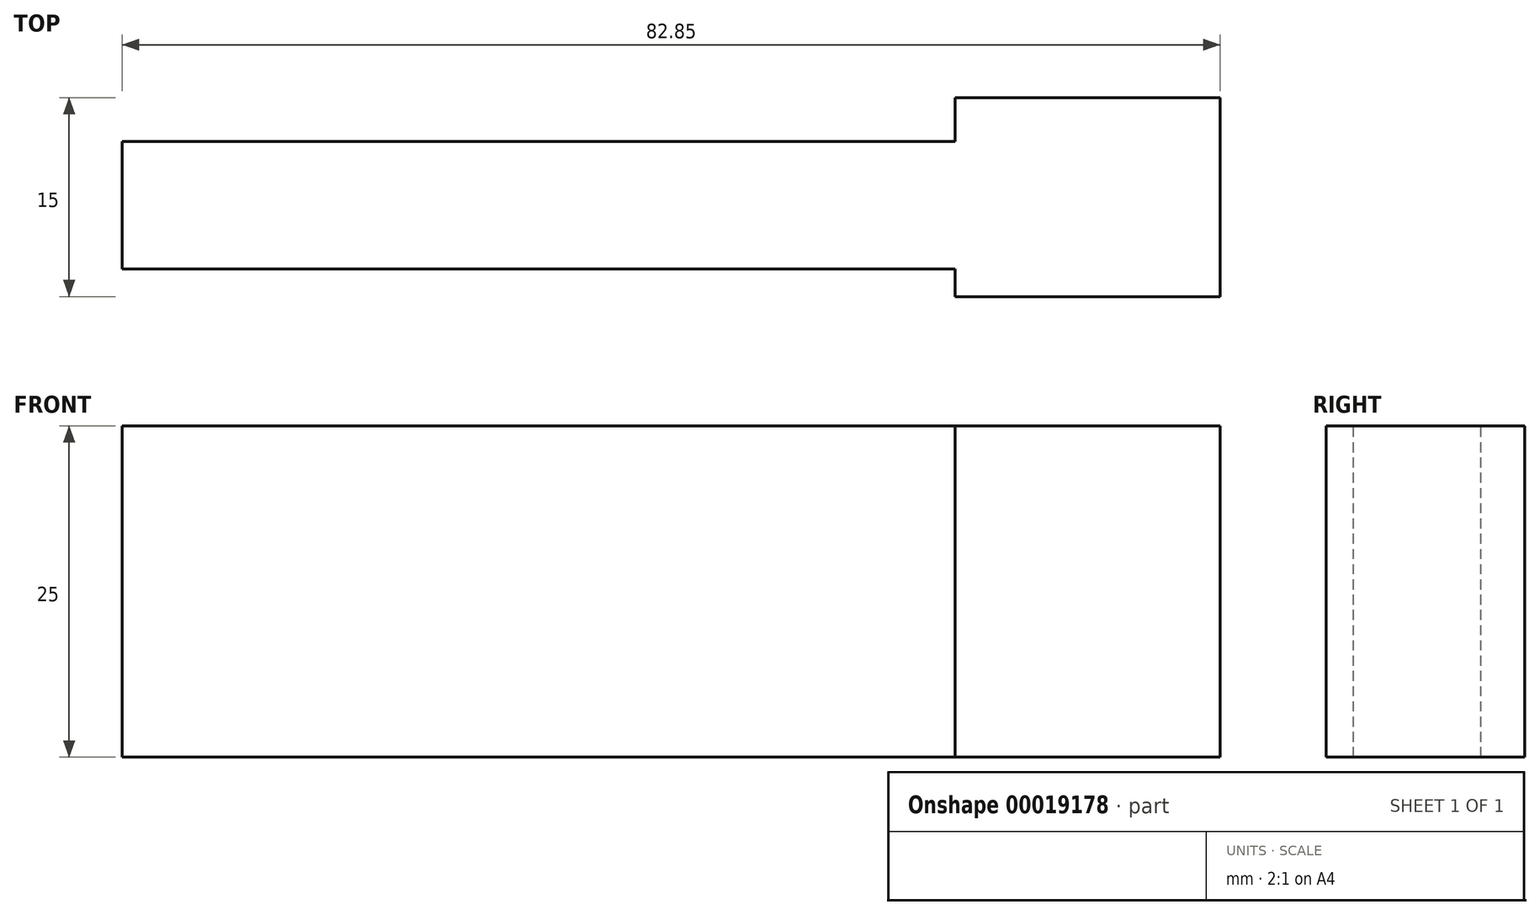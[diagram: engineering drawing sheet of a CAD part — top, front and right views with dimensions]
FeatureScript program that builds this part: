
annotation { "Feature Type Name" : "Feature", "Feature Type Description" : "" }
export const myFeature = defineFeature(function(context is Context, id is Id, definition is map)
    precondition{}
    {
        {
            var Q0;
            Q0=qCreatedBy(makeId("Top.planeOp"),FACE);
            var sketch = newSketch(context, id + "F0", { "sketchPlane" : qUnion([Q0])});
            skLineSegment(sketch, "E0.bottom", {"start": v(-30.27, -19.76) * mm, "end": v(-10.27, -19.76) * mm});
            skLineSegment(sketch, "E0.top", {"start": v(-30.27, -34.76) * mm, "end": v(-10.27, -34.76) * mm});
            skLineSegment(sketch, "E0.left", {"start": v(-30.27, -19.76) * mm, "end": v(-30.27, -34.76) * mm});
            skLineSegment(sketch, "E0.right", {"start": v(-10.27, -19.76) * mm, "end": v(-10.27, -34.76) * mm});
            skSolve(sketch);
        }
        {
            var Q0;
            Q0=makeQuery(id+"F0.imprint","IMPRINT",FACE,{"disambiguationData":[TD([[makeQuery(id+"F0.imprint","IMPRINT",EDGE,{"derivedFrom":sQuery(id+"F0.wireOp",EDGE,"E0.bottom")}),-1.0]])]});
            var sketch = newSketch(context, id + "F1", { "sketchPlane" : qUnion([Q0])});
            skLineSegment(sketch, "E1.bottom", {"start": v(-93.12, -23.06) * mm, "end": v(-12.85, -23.06) * mm});
            skLineSegment(sketch, "E1.top", {"start": v(-93.12, -32.68) * mm, "end": v(-12.85, -32.68) * mm});
            skLineSegment(sketch, "E1.left", {"start": v(-93.12, -23.06) * mm, "end": v(-93.12, -32.68) * mm});
            skLineSegment(sketch, "E1.right", {"start": v(-12.85, -23.06) * mm, "end": v(-12.85, -32.68) * mm});
            skSolve(sketch);
        }
        {
            var Q0;
            Q0 = qSketchRegion(id + "F0", true);
            extrude(context, id + "F2", {"entities" : qUnion([Q0]), "depth" : 25 * mm});
        }
        {
            var Q0;
            Q0 = qSketchRegion(id + "F1", true);
            extrude(context, id + "F3", {"entities" : qUnion([Q0]), "operationType" : NewBodyOperationType.ADD, "depth" : 25 * mm});
        }
        {
            var Q0;
            Q0 = qSketchRegion(id + "F1", true);
            extrude(context, id + "F4", {"entities" : qUnion([Q0]), "operationType" : NewBodyOperationType.ADD, "depth" : 25 * mm});
        }
    });
